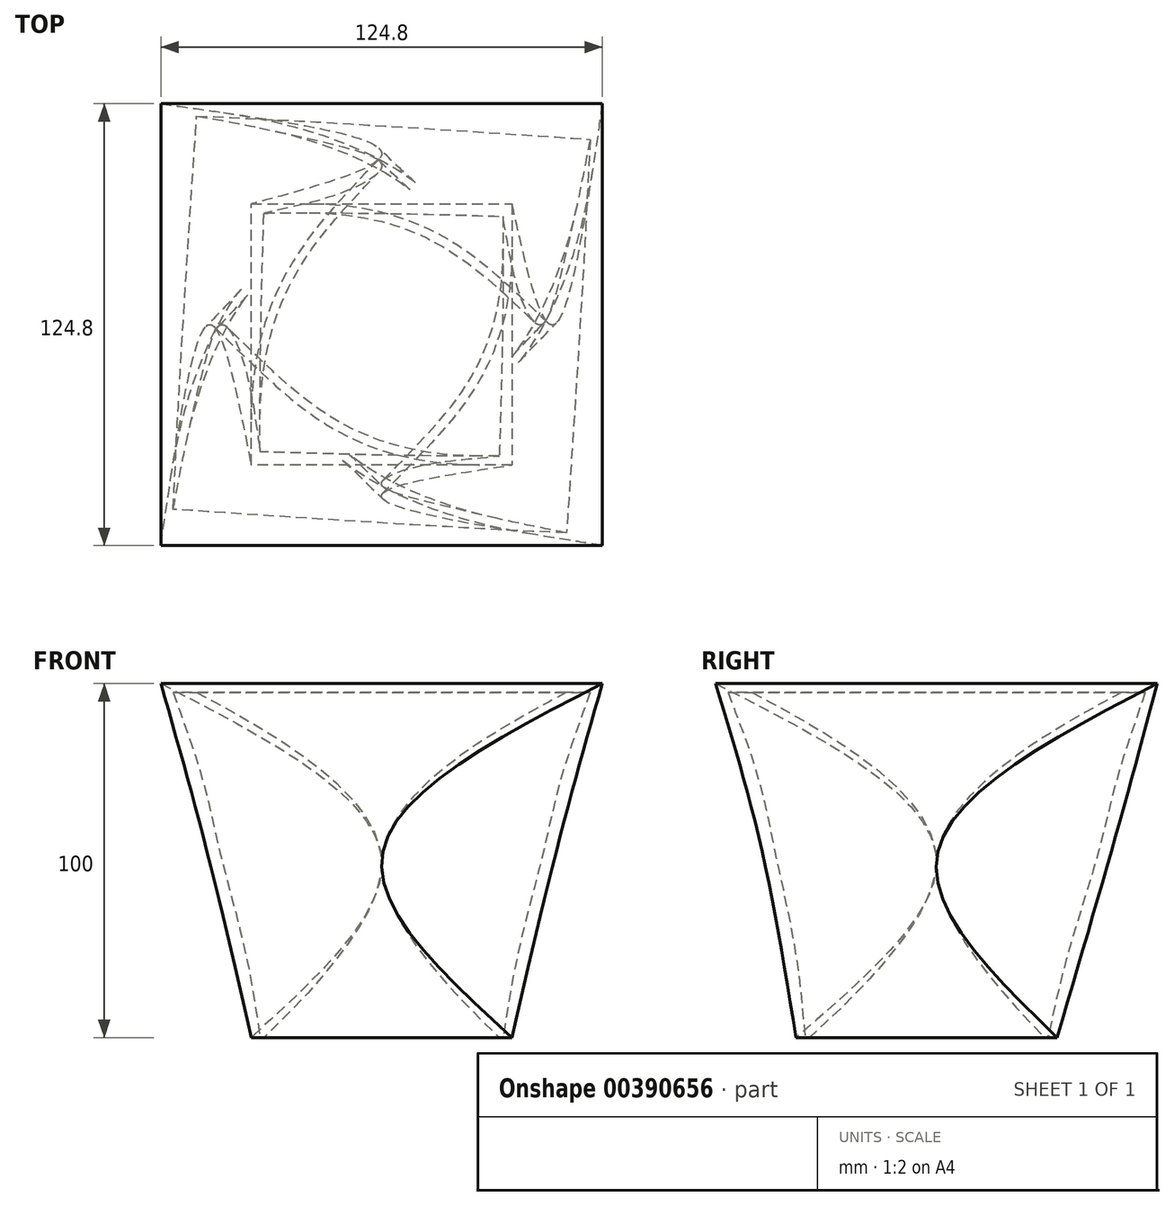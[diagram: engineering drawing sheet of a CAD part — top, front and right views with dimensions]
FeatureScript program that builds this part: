
annotation { "Feature Type Name" : "Feature", "Feature Type Description" : "" }
export const myFeature = defineFeature(function(context is Context, id is Id, definition is map)
    precondition{}
    {
        {
            var Q0;
            Q0=qCreatedBy(makeId("Top.planeOp"),FACE);
            cPlane(context, id + "F0", {"entities" : qUnion([Q0]), "cplaneType" : CPlaneType.OFFSET, "offset" : 100 * mm, "width" : 152.4 * mm, "height" : 152.4 * mm});
        }
        {
            var Q0;
            Q0=qCreatedBy(makeId("Top.planeOp"),FACE);
            var sketch = newSketch(context, id + "F1", { "sketchPlane" : qUnion([Q0])});
            skCircle(sketch, "E0.cCircle", {"center": v(0, -2.78) * mm, "radius": 36.86 * mm, "construction": true});
            skLineSegment(sketch, "E0.0", {"start": v(36.86, -39.64) * mm, "end": v(-36.86, -39.64) * mm});
            skLineSegment(sketch, "E0.1", {"start": v(-36.86, -39.64) * mm, "end": v(-36.86, 34.08) * mm});
            skLineSegment(sketch, "E0.2", {"start": v(-36.86, 34.08) * mm, "end": v(36.86, 34.08) * mm});
            skLineSegment(sketch, "E0.3", {"start": v(36.86, 34.08) * mm, "end": v(36.86, -39.64) * mm});
            skPoint(sketch, "E0.0.midPoint", {"position": v(0, -39.64) * mm});
            skSolve(sketch);
        }
        {
            var Q0;
            Q0=qCreatedBy(id+"F0.planeOp",FACE);
            var sketch = newSketch(context, id + "F2", { "sketchPlane" : qUnion([Q0])});
            skCircle(sketch, "E1.cCircle", {"center": v(0, 0) * mm, "radius": 62.4 * mm, "construction": true});
            skLineSegment(sketch, "E1.0", {"start": v(62.4, -62.4) * mm, "end": v(-62.4, -62.4) * mm});
            skLineSegment(sketch, "E1.1", {"start": v(-62.4, -62.4) * mm, "end": v(-62.4, 62.4) * mm});
            skLineSegment(sketch, "E1.2", {"start": v(-62.4, 62.4) * mm, "end": v(62.4, 62.4) * mm});
            skLineSegment(sketch, "E1.3", {"start": v(62.4, 62.4) * mm, "end": v(62.4, -62.4) * mm});
            skPoint(sketch, "E1.0.midPoint", {"position": v(0, -62.4) * mm});
            skSolve(sketch);
        }
        {
            var Q0;
            Q0=qCreatedBy(makeId("Top.planeOp"),FACE);
            cPlane(context, id + "F3", {"entities" : qUnion([Q0]), "cplaneType" : CPlaneType.OFFSET, "offset" : 50 * mm, "width" : 150 * mm, "height" : 150 * mm});
        }
        {
            var Q0;
            Q0=qCreatedBy(id+"F3.planeOp",FACE);
            var sketch = newSketch(context, id + "F4", { "sketchPlane" : qUnion([Q0])});
            skCircle(sketch, "E2.cCircle", {"center": v(0, 0) * mm, "radius": 34.44 * mm, "construction": true});
            skLineSegment(sketch, "E2.0", {"start": v(0, -48.7) * mm, "end": v(-48.7, 0) * mm});
            skLineSegment(sketch, "E2.1", {"start": v(-48.7, 0) * mm, "end": v(0, 48.7) * mm});
            skLineSegment(sketch, "E2.2", {"start": v(0, 48.7) * mm, "end": v(48.7, 0) * mm});
            skLineSegment(sketch, "E2.3", {"start": v(48.7, 0) * mm, "end": v(0, -48.7) * mm});
            skPoint(sketch, "E2.0.midPoint", {"position": v(-24.35, -24.35) * mm});
            skSolve(sketch);
        }
        {
            var Q0;
            Q0=makeQuery(id+"F2.imprint","IMPRINT",FACE,{"disambiguationData":[TD([[makeQuery(id+"F2.imprint","IMPRINT",EDGE,{"derivedFrom":sQuery(id+"F2.wireOp",EDGE,"E1.0")}),-1.0]])]});
            var Q1;
            Q1=makeQuery(id+"F4.imprint","IMPRINT",FACE,{"disambiguationData":[TD([[makeQuery(id+"F4.imprint","IMPRINT",EDGE,{"derivedFrom":sQuery(id+"F4.wireOp",EDGE,"E2.0")}),-1.0]])]});
            var Q2;
            Q2=makeQuery(id+"F1.imprint","IMPRINT",FACE,{"disambiguationData":[TD([[makeQuery(id+"F1.imprint","IMPRINT",EDGE,{"derivedFrom":sQuery(id+"F1.wireOp",EDGE,"E0.0")}),-1.0]])]});
            loft(context, id + "F5", {"sheetProfilesArray" : [{ "sheetProfileEntities" : qUnion([Q0]) }, { "sheetProfileEntities" : qUnion([Q1]) }, { "sheetProfileEntities" : qUnion([Q2]) }]});
        }
        {
            var Q0;
            Q0=makeQuery(id+"F5.opLoft","CAP_FACE",FACE,{"disambiguationData":[OSD([makeQuery(id+"F1.imprint","IMPRINT",FACE,{"disambiguationData":[TD([[makeQuery(id+"F1.imprint","IMPRINT",EDGE,{"derivedFrom":sQuery(id+"F1.wireOp",EDGE,"E0.0")}),-1.0]])]})])],"isStart":true});
            shell(context, id + "F6", {"entities" : qUnion([Q0]), "thickness" : 2.5 * mm});
        }
    });
